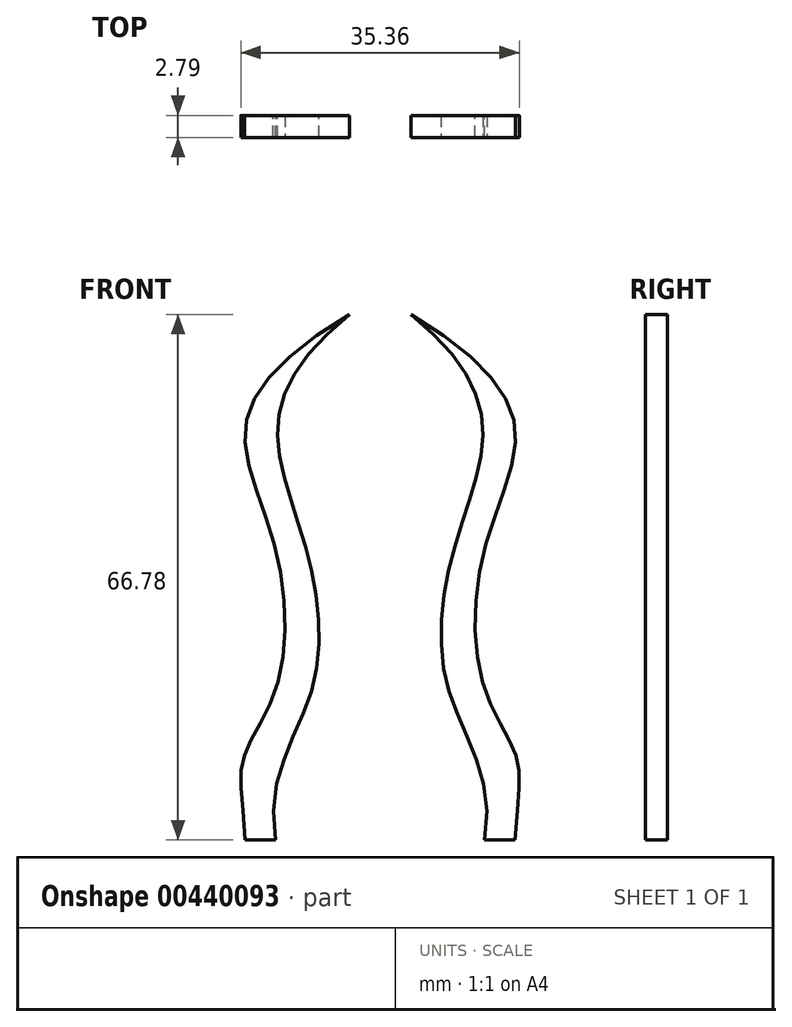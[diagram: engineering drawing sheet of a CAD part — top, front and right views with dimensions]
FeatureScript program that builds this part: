
annotation { "Feature Type Name" : "Feature", "Feature Type Description" : "" }
export const myFeature = defineFeature(function(context is Context, id is Id, definition is map)
    precondition{}
    {
        {
            var Q0;
            Q0=qCreatedBy(makeId("Front.planeOp"),FACE);
            var sketch = newSketch(context, id + "F0", { "sketchPlane" : qUnion([Q0])});
            skFitSpline(sketch, "E0", {"points": [v(-13.27, 0) * mm, v(-8.68, 19.1) * mm, v(-9.38, 36.95) * mm, v(-13.04, 52.34) * mm, v(-3.91, 66.78) * mm], "startDerivative": vector(-16.9, 91.1) * mm, "endDerivative": vector(72.35, 58.42) * mm});
            skFitSpline(sketch, "E1", {"points": [v(-17.15, 0) * mm, v(-17.27, 10.73) * mm, v(-13.27, 19.1) * mm, v(-13.27, 36.95) * mm, v(-17.15, 52.34) * mm, v(-3.91, 66.78) * mm], "startDerivative": vector(-5.58, 101) * mm, "endDerivative": vector(103.7, 62.72) * mm});
            skFitSpline(sketch, "E2.MirrorCS", {"points": [v(13.27, 0) * mm, v(8.68, 19.1) * mm, v(9.38, 36.95) * mm, v(13.04, 52.34) * mm, v(3.91, 66.78) * mm], "startDerivative": vector(16.9, 91.1) * mm, "endDerivative": vector(-72.35, 58.42) * mm});
            skFitSpline(sketch, "E3.MirrorCS", {"points": [v(17.15, 0) * mm, v(17.27, 10.73) * mm, v(13.27, 19.1) * mm, v(13.27, 36.95) * mm, v(17.15, 52.34) * mm, v(3.91, 66.78) * mm], "startDerivative": vector(5.58, 101) * mm, "endDerivative": vector(-103.7, 62.72) * mm});
            skLineSegment(sketch, "E4", {"start": v(17.15, 0) * mm, "end": v(13.27, 0) * mm});
            skLineSegment(sketch, "E5", {"start": v(-13.27, 0) * mm, "end": v(-17.15, 0) * mm});
            skSolve(sketch);
        }
        {
            var Q0;
            Q0 = qSketchRegion(id + "F0", true);
            extrude(context, id + "F1", {"entities" : qUnion([Q0]), "depth" : 2.8 * mm});
        }
    });
